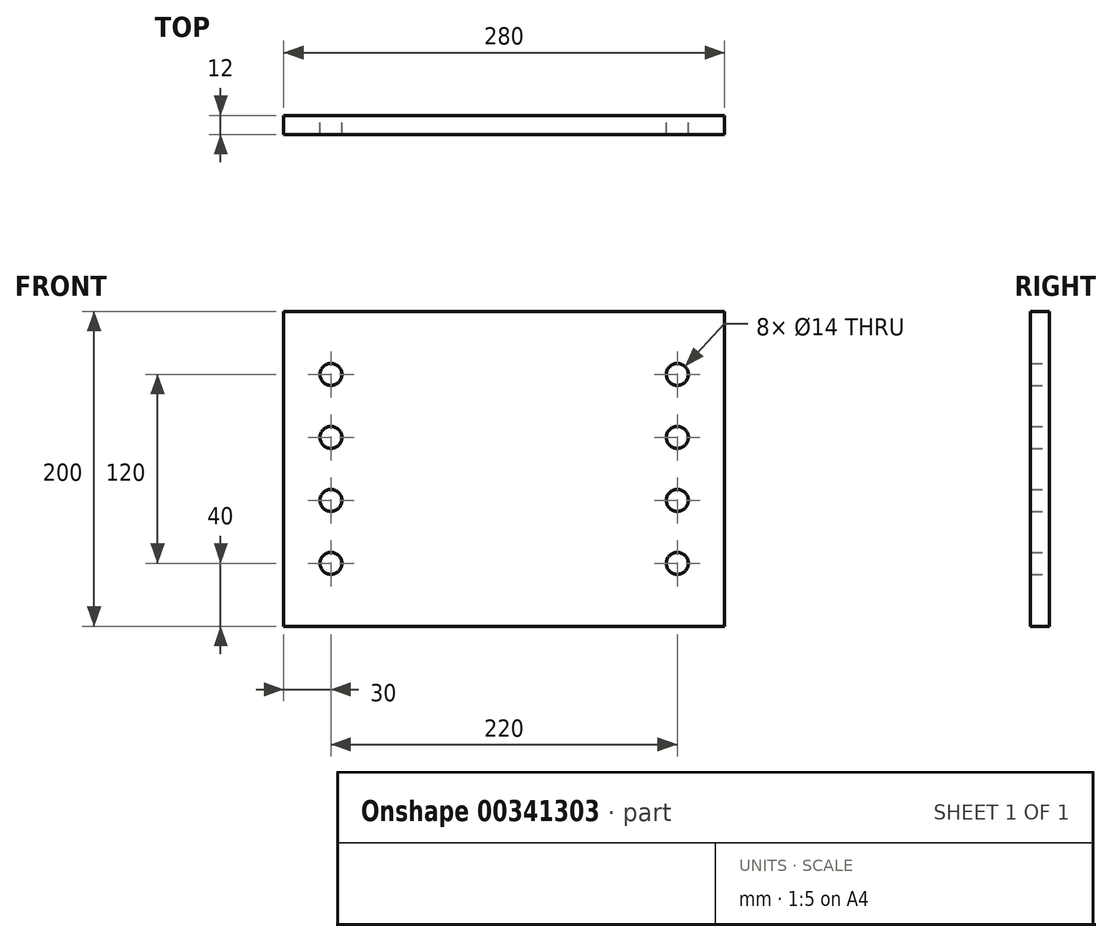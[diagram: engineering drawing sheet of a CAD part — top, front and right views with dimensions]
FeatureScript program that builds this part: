
annotation { "Feature Type Name" : "Feature", "Feature Type Description" : "" }
export const myFeature = defineFeature(function(context is Context, id is Id, definition is map)
    precondition{}
    {
        {
            var Q0;
            Q0=qCreatedBy(makeId("Front.planeOp"),FACE);
            var sketch = newSketch(context, id + "F0", { "sketchPlane" : qUnion([Q0])});
            skLineSegment(sketch, "E0.bottom", {"start": v(0, 0) * mm, "end": v(280, 0) * mm});
            skLineSegment(sketch, "E0.top", {"start": v(0, 200) * mm, "end": v(280, 200) * mm});
            skLineSegment(sketch, "E0.left", {"start": v(0, 0) * mm, "end": v(0, 200) * mm});
            skLineSegment(sketch, "E0.right", {"start": v(280, 0) * mm, "end": v(280, 200) * mm});
            skSolve(sketch);
        }
        {
            var Q0;
            Q0=makeQuery(id+"F0.imprint","IMPRINT",FACE,{"disambiguationData":[TD([[makeQuery(id+"F0.imprint","IMPRINT",EDGE,{"derivedFrom":sQuery(id+"F0.wireOp",EDGE,"E0.bottom")}),1.0]])]});
            extrude(context, id + "F1", {"entities" : qUnion([Q0]), "depth" : 12 * mm});
        }
        {
            var Q0;
            Q0=makeQuery(id+"F1.opExtrude","CAP_FACE",FACE,{"disambiguationData":[OSD([sQuery(id+"F0.wireOp",EDGE,"E0.bottom"),sQuery(id+"F0.wireOp",EDGE,"E0.top"),sQuery(id+"F0.wireOp",EDGE,"E0.left"),sQuery(id+"F0.wireOp",EDGE,"E0.right")])],"isStart":false});
            var sketch = newSketch(context, id + "F2", { "sketchPlane" : qUnion([Q0])});
            skLineSegment(sketch, "E1", {"start": v(30, 200) * mm, "end": v(30, 0) * mm});
            skLineSegment(sketch, "E2", {"start": v(250, 200) * mm, "end": v(250, 0) * mm});
            skLineSegment(sketch, "E3", {"start": v(0, 160) * mm, "end": v(280, 160) * mm});
            skLineSegment(sketch, "E4", {"start": v(0, 120) * mm, "end": v(280, 120) * mm});
            skLineSegment(sketch, "E5", {"start": v(0, 80) * mm, "end": v(280, 80) * mm});
            skLineSegment(sketch, "E6", {"start": v(0, 40) * mm, "end": v(280, 40) * mm});
            skPoint(sketch, "E7", {"position": v(30, 160) * mm});
            skPoint(sketch, "E8", {"position": v(30, 120) * mm});
            skPoint(sketch, "E9", {"position": v(30, 80) * mm});
            skPoint(sketch, "E10", {"position": v(30, 40) * mm});
            skPoint(sketch, "E11", {"position": v(250, 40) * mm});
            skPoint(sketch, "E12", {"position": v(250, 80) * mm});
            skPoint(sketch, "E13", {"position": v(250, 120) * mm});
            skPoint(sketch, "E14", {"position": v(250, 160) * mm});
            skSolve(sketch);
        }
        {
            var Q0;
            Q0=sQuery(id+"F2.wireOp",VERTEX,"E7");
            var Q1;
            Q1=sQuery(id+"F2.wireOp",VERTEX,"E8");
            var Q2;
            Q2=sQuery(id+"F2.wireOp",VERTEX,"E9");
            var Q3;
            Q3=sQuery(id+"F2.wireOp",VERTEX,"E10");
            var Q4;
            Q4=sQuery(id+"F2.wireOp",VERTEX,"E11");
            var Q5;
            Q5=sQuery(id+"F2.wireOp",VERTEX,"E12");
            var Q6;
            Q6=sQuery(id+"F2.wireOp",VERTEX,"E13");
            var Q7;
            Q7=sQuery(id+"F2.wireOp",VERTEX,"E14");
            var Q8;
            Q8=makeQuery(id+"F1.opExtrude","SWEPT_BODY",BODY,{"disambiguationData":[OSD([sQuery(id+"F0.wireOp",EDGE,"E0.bottom"),sQuery(id+"F0.wireOp",EDGE,"E0.top"),sQuery(id+"F0.wireOp",EDGE,"E0.left"),sQuery(id+"F0.wireOp",EDGE,"E0.right")])]});
            hole(context, id + "F3", {"style" : HoleStyle.SIMPLE, "endStyle" : HoleEndStyle.THROUGH, "holeDiameter" : 14 * mm, "tappedDepth" : 12 * mm, "tapClearance" : 3, "locations" : qUnion([Q0, Q1, Q2, Q3, Q4, Q5, Q6, Q7]), "scope" : qUnion([Q8]), "startStyle" : HoleStartStyle.PART});
        }
    });
